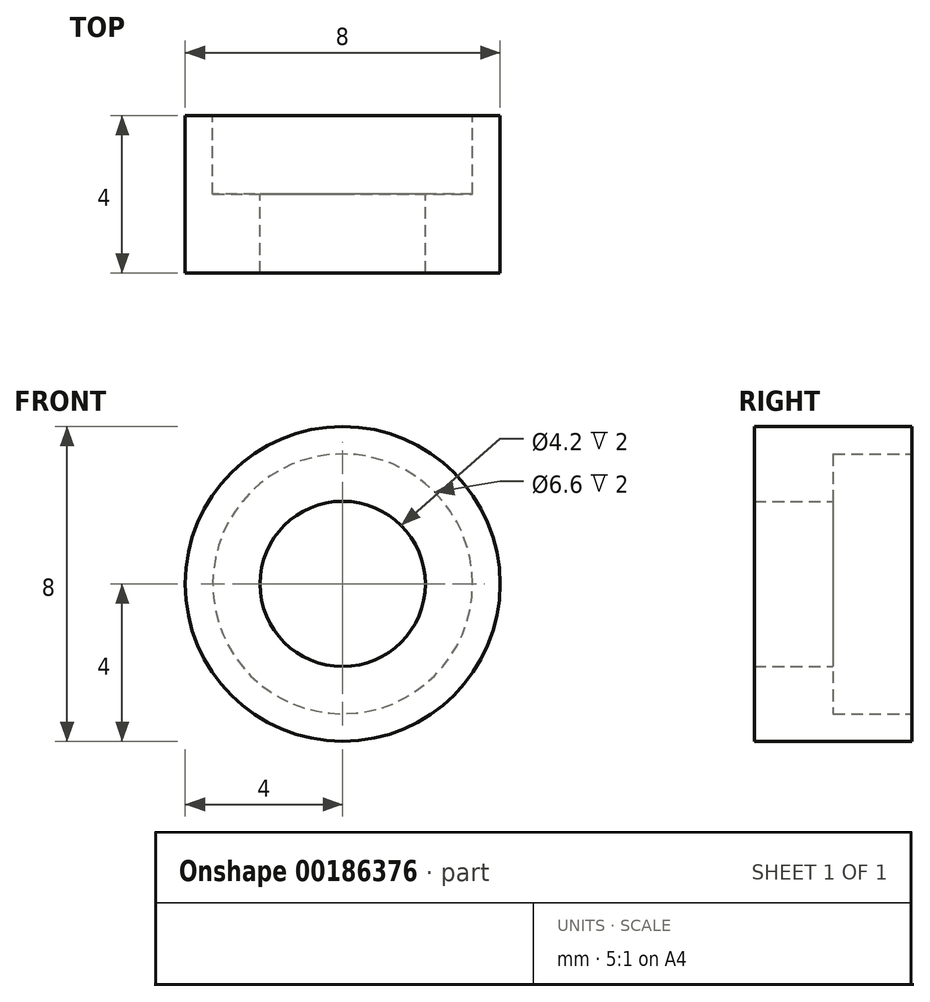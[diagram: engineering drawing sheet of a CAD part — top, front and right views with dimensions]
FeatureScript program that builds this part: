
annotation { "Feature Type Name" : "Feature", "Feature Type Description" : "" }
export const myFeature = defineFeature(function(context is Context, id is Id, definition is map)
    precondition{}
    {
        {
            var Q0;
            Q0=qCreatedBy(makeId("Right.planeOp"),FACE);
            var sketch = newSketch(context, id + "F0", { "sketchPlane" : qUnion([Q0])});
            skLineSegment(sketch, "E0", {"start": v(11.47, 0) * mm, "end": v(0, 0) * mm, "construction": true});
            skLineSegment(sketch, "E1", {"start": v(2, 2.1) * mm, "end": v(0, 2.1) * mm});
            skLineSegment(sketch, "E2", {"start": v(2, 2.1) * mm, "end": v(2, 3.3) * mm});
            skLineSegment(sketch, "E3", {"start": v(4, 3.3) * mm, "end": v(2, 3.3) * mm});
            skLineSegment(sketch, "E4", {"start": v(4, 3.3) * mm, "end": v(4, 4) * mm});
            skLineSegment(sketch, "E5", {"start": v(0, 4) * mm, "end": v(4, 4) * mm});
            skLineSegment(sketch, "E6", {"start": v(0, 0) * mm, "end": v(0, 4) * mm});
            skLineSegment(sketch, "E7", {"start": v(0, 0) * mm, "end": v(0, 0) * mm});
            skLineSegment(sketch, "E8", {"start": v(0, 2.1) * mm, "end": v(0, 0) * mm});
            skSolve(sketch);
        }
        {
            var Q0;
            Q0=makeQuery(id+"F0.imprint","IMPRINT",FACE,{"disambiguationData":[TD([[makeQuery(id+"F0.imprint","IMPRINT",EDGE,{"derivedFrom":sQuery(id+"F0.wireOp",EDGE,"E1")}),-1.0]])]});
            var Q1;
            Q1=sQuery(id+"F0.wireOp",EDGE,"E0");
            revolve(context, id + "F1", {"entities" : qUnion([Q0]), "axis" : qUnion([Q1]), "revolveType" : RevolveType.FULL});
        }
    });
